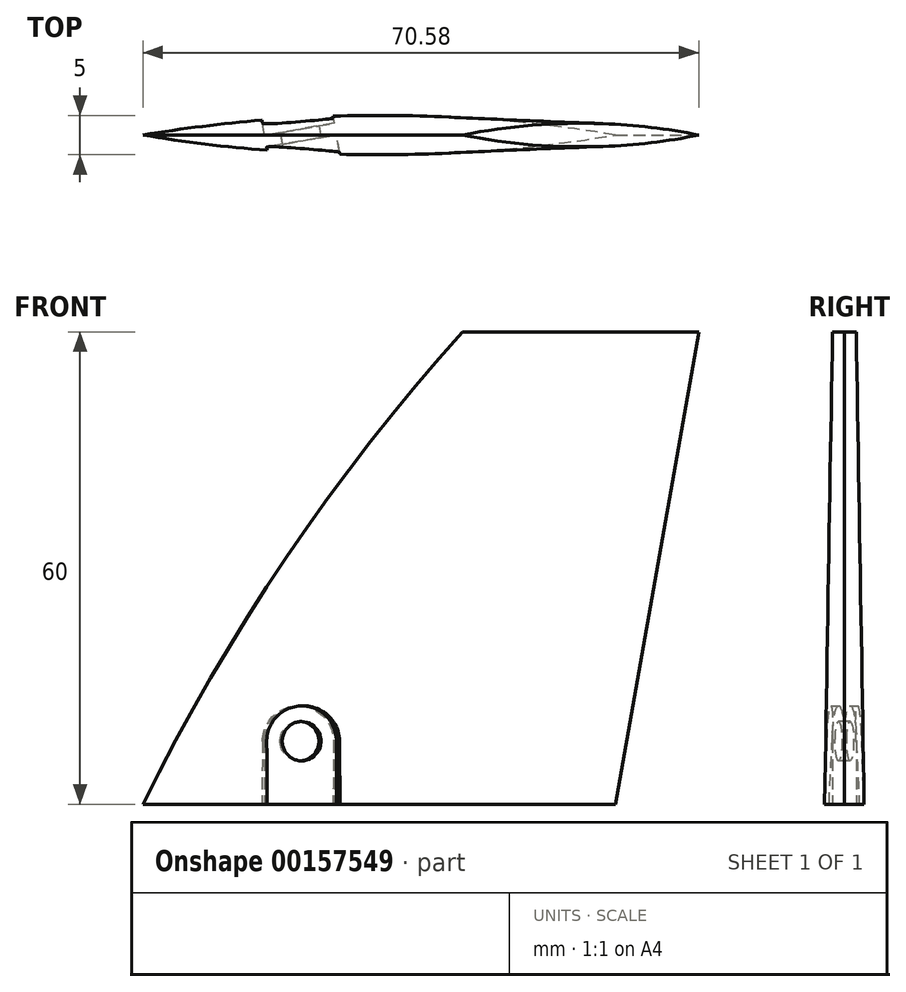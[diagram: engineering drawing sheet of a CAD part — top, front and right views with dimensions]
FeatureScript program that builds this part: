
annotation { "Feature Type Name" : "Feature", "Feature Type Description" : "" }
export const myFeature = defineFeature(function(context is Context, id is Id, definition is map)
    precondition{}
    {
        {
            assignVariable(context, id + "F0", {"name" : "span", "anyValue" : 60});
        }
        {
            var Q0;
            Q0=qCreatedBy(makeId("Top.planeOp"),FACE);
            cPlane(context, id + "F1", {"entities" : qUnion([Q0]), "cplaneType" : CPlaneType.OFFSET, "offset" : getVariable(context, 'span') * mm, "width" : 150 * mm, "height" : 150 * mm});
        }
        {
            var Q0;
            Q0=qCreatedBy(makeId("Top.planeOp"),FACE);
            var sketch = newSketch(context, id + "F2", { "sketchPlane" : qUnion([Q0])});
            skArc(sketch, "E0", {"start": v(-29.78, 0) * mm, "mid": v(0.22, -2.5) * mm, "end": v(30.22, 0) * mm});
            skLineSegment(sketch, "E1", {"start": v(-29.78, 0) * mm, "end": v(30.22, 0) * mm, "construction": true});
            skArc(sketch, "E2.MirrorCS", {"start": v(-29.78, 0) * mm, "mid": v(0.22, 2.5) * mm, "end": v(30.22, 0) * mm});
            skSolve(sketch);
        }
        {
            var Q0;
            Q0=qCreatedBy(makeId("Front.planeOp"),FACE);
            var sketch = newSketch(context, id + "F3", { "sketchPlane" : qUnion([Q0])});
            skLineSegment(sketch, "E3", {"start": v(30.22, 0) * mm, "end": v(40.8, 60) * mm});
            skSolve(sketch);
        }
        {
            var Q0;
            Q0=qCreatedBy(id+"F1.planeOp",FACE);
            var sketch = newSketch(context, id + "F4", { "sketchPlane" : qUnion([Q0])});
            skLineSegment(sketch, "E4", {"start": v(10.8, 0) * mm, "end": v(40.8, 0) * mm, "construction": true});
            skArc(sketch, "E5", {"start": v(10.8, 0) * mm, "mid": v(25.8, -1.5) * mm, "end": v(40.8, 0) * mm});
            skArc(sketch, "E6.MirrorCS", {"start": v(10.8, 0) * mm, "mid": v(25.8, 1.5) * mm, "end": v(40.8, 0) * mm});
            skSolve(sketch);
        }
        {
            var Q0;
            Q0=qCreatedBy(makeId("Front.planeOp"),FACE);
            var sketch = newSketch(context, id + "F5", { "sketchPlane" : qUnion([Q0])});
            skArc(sketch, "E7", {"start": v(10.8, 60) * mm, "mid": v(-11.56, 31.4) * mm, "end": v(-29.78, 0) * mm});
            skLineSegment(sketch, "E8", {"start": v(10.8, 60) * mm, "end": v(-29.78, 0) * mm, "construction": true});
            skSolve(sketch);
        }
        {
            var Q0;
            Q0=makeQuery(id+"F2.imprint","IMPRINT",FACE,{"disambiguationData":[TD([[makeQuery(id+"F2.imprint","IMPRINT",EDGE,{"derivedFrom":sQuery(id+"F2.wireOp",EDGE,"E0")}),1.0]])]});
            var Q1;
            Q1=makeQuery(id+"F4.imprint","IMPRINT",FACE,{"disambiguationData":[TD([[makeQuery(id+"F4.imprint","IMPRINT",EDGE,{"derivedFrom":sQuery(id+"F4.wireOp",EDGE,"E5")}),1.0]])]});
            var Q2;
            Q2=sQuery(id+"F5.wireOp",EDGE,"E7");
            var Q3;
            Q3=sQuery(id+"F3.wireOp",EDGE,"E3");
            loft(context, id + "F6", {"addGuides" : true, "sheetProfilesArray" : [{ "sheetProfileEntities" : qUnion([Q0]) }, { "sheetProfileEntities" : qUnion([Q1]) }], "guidesArray" : [{ "guideEntities" : qUnion([Q2]), "guideDerivativeType" : LoftGuideDerivativeType.DEFAULT, "guideDerivativeMagnitude" : 1 }, { "guideEntities" : qUnion([Q3]), "guideDerivativeType" : LoftGuideDerivativeType.DEFAULT, "guideDerivativeMagnitude" : 1 }]});
        }
        {
            var Q0;
            Q0=qCreatedBy(makeId("Front.planeOp"),FACE);
            var sketch = newSketch(context, id + "F7", { "sketchPlane" : qUnion([Q0])});
            skLineSegment(sketch, "E9", {"start": v(-9.78, 0) * mm, "end": v(-9.78, 43.47) * mm, "construction": true});
            skSolve(sketch);
        }
        {
            var Q0;
            Q0=sQuery(id+"F7.wireOp",EDGE,"E9");
            cPlane(context, id + "F8", {"entities" : qUnion([Q0]), "cplaneType" : CPlaneType.LINE_ANGLE, "offset" : 25 * mm, "angle" : 100 * degree, "width" : 150 * mm, "height" : 150 * mm});
        }
        {
            var Q0;
            Q0=qCreatedBy(id+"F8.planeOp",FACE);
            var sketch = newSketch(context, id + "F9", { "sketchPlane" : qUnion([Q0])});
            skArc(sketch, "E10", {"start": v(14.13, 8) * mm, "mid": v(9.63, 12.5) * mm, "end": v(5.13, 8) * mm});
            skLineSegment(sketch, "E11", {"start": v(14.13, 8) * mm, "end": v(14.13, 0) * mm});
            skLineSegment(sketch, "E12", {"start": v(5.13, 8) * mm, "end": v(5.13, 0) * mm});
            skLineSegment(sketch, "E13", {"start": v(5.13, 0) * mm, "end": v(14.13, 0) * mm});
            skCircle(sketch, "E14", {"center": v(9.63, 8) * mm, "radius": 2.5 * mm});
            skSolve(sketch);
        }
        {
            var Q0;
            Q0=makeQuery(id+"F9.imprint","IMPRINT",FACE,{"disambiguationData":[TD([[makeQuery(id+"F9.imprint","IMPRINT",EDGE,{"derivedFrom":sQuery(id+"F9.wireOp",EDGE,"E10")}),1.0]])]});
            var Q1;
            Q1=makeQuery(id+"F9.imprint","IMPRINT",FACE,{"disambiguationData":[TD([[makeQuery(id+"F9.imprint","IMPRINT",EDGE,{"derivedFrom":sQuery(id+"F9.wireOp",EDGE,"E14")}),1.0]])]});
            extrude(context, id + "F10", {"entities" : qUnion([Q0, Q1]), "operationType" : NewBodyOperationType.REMOVE, "endBound" : BoundingType.THROUGH_ALL, "oppositeDirection" : true, "depth" : 25 * mm, "hasSecondDirection" : true, "secondDirectionBound" : SecondDirectionBoundingType.THROUGH_ALL, "secondDirectionOppositeDirection" : false, "secondDirectionDepth" : 25 * mm});
        }
        {
            var Q0;
            Q0 = qSketchRegion(id + "F9", true);
            extrude(context, id + "F11", {"entities" : qUnion([Q0]), "operationType" : NewBodyOperationType.ADD, "endBound" : BoundingType.SYMMETRIC, "depth" : 1.5 * mm});
        }
    });
